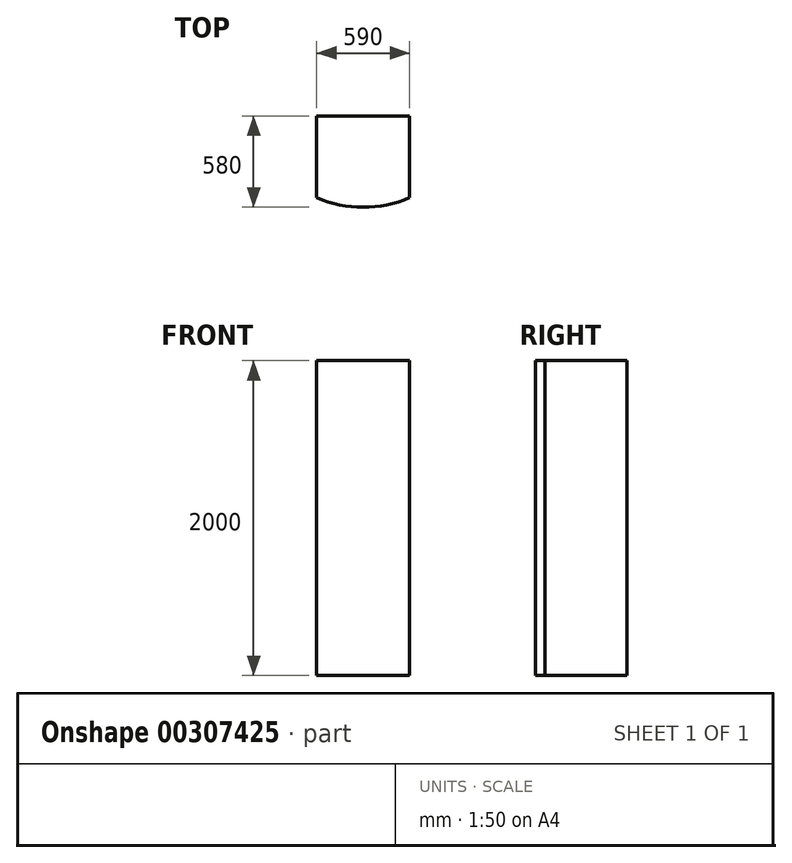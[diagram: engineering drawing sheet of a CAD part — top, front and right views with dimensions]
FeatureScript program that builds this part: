
annotation { "Feature Type Name" : "Feature", "Feature Type Description" : "" }
export const myFeature = defineFeature(function(context is Context, id is Id, definition is map)
    precondition{}
    {
        {
            var Q0;
            Q0=qCreatedBy(makeId("Front.planeOp"),FACE);
            var sketch = newSketch(context, id + "F0", { "sketchPlane" : qUnion([Q0])});
            skLineSegment(sketch, "E0.bottom", {"start": v(0, 0) * mm, "end": v(590, 0) * mm});
            skLineSegment(sketch, "E0.top", {"start": v(0, 2000) * mm, "end": v(590, 2000) * mm});
            skLineSegment(sketch, "E0.left", {"start": v(0, 0) * mm, "end": v(0, 2000) * mm});
            skLineSegment(sketch, "E0.right", {"start": v(590, 0) * mm, "end": v(590, 2000) * mm});
            skSolve(sketch);
        }
        {
            var Q0;
            Q0=makeQuery(id+"F0.imprint","IMPRINT",FACE,{"disambiguationData":[TD([[makeQuery(id+"F0.imprint","IMPRINT",EDGE,{"derivedFrom":sQuery(id+"F0.wireOp",EDGE,"E0.bottom")}),1.0]])]});
            extrude(context, id + "F1", {"entities" : qUnion([Q0]), "depth" : 580 * mm, "offsetDistance" : 25 * mm});
        }
        {
            var Q0;
            Q0=makeQuery(id+"F1.opExtrude","SWEPT_FACE",FACE,{"disambiguationData":[OSD([sQuery(id+"F0.wireOp",EDGE,"E0.top")])]});
            var sketch = newSketch(context, id + "F2", { "sketchPlane" : qUnion([Q0])});
            skLineSegment(sketch, "E1", {"start": v(0, -520) * mm, "end": v(590, -520) * mm});
            skPoint(sketch, "E2", {"position": v(295, -580) * mm});
            skArc(sketch, "E3", {"start": v(0, -520) * mm, "mid": v(295, -580) * mm, "end": v(590, -520) * mm});
            skSolve(sketch);
        }
        {
            var Q0;
            Q0 = qSketchRegion(id + "F2", true);
            var Q1;
            {var subQ0=sQuery(id+"F2.wireOp",EDGE,"E1");Q1=makeQuery(id+"F2.imprint","IMPRINT",FACE,{"disambiguationData":[TD([[makeQuery(id+"F2.imprint","IMPRINT",EDGE,{"derivedFrom":subQ0}),1.0]])]});}
            extrude(context, id + "F3", {"entities" : qUnion([Q0, Q1]), "operationType" : NewBodyOperationType.INTERSECT, "endBound" : BoundingType.UP_TO_NEXT, "oppositeDirection" : true, "depth" : 25 * mm, "offsetDistance" : 25 * mm});
        }
    });
